AUTODESK INVENTOR PART (.ipt)
format: ipt  version: 2023.5 (Build 275446000, 446)  size: 140,288 bytes
history: native  units: in
note: dims shown in document units (in); Inventor stores cm internally (conversion verified against a paired STEP export)
features: sketch x2
ambient origin geometry x8: Origin, YZ Plane, XZ Plane, XY Plane, X Axis, Y Axis, Z Axis, Center Point
feature tree (2):
  sketch  "Sketch1"  dims[d0=24.0in]
  sketch  "Sketch2"  dims[d2=2.6in d3=1.5in d4=7.315in d5=5.75in d6=34.75in d7=2.0in d8=17.0in d9=2.75in d10=4.38in d12=2.0in d13=41.625in d14=6.0in d15=8.25in d16=4.0in d17=3.0in d18=4.812in d20=25.0in d29=3.125in d31=29.85in d32=3.4in d33=6.0in d34=4.0in d35=3.0in d38=6.0in d43=7.315in d44=24.0in d45=2.6in d46=1.5in d47=10.0in d48=4.0in d49=6.5in d50=5.0in d52=2.0in d54=2.5in d55=0.7559in]
